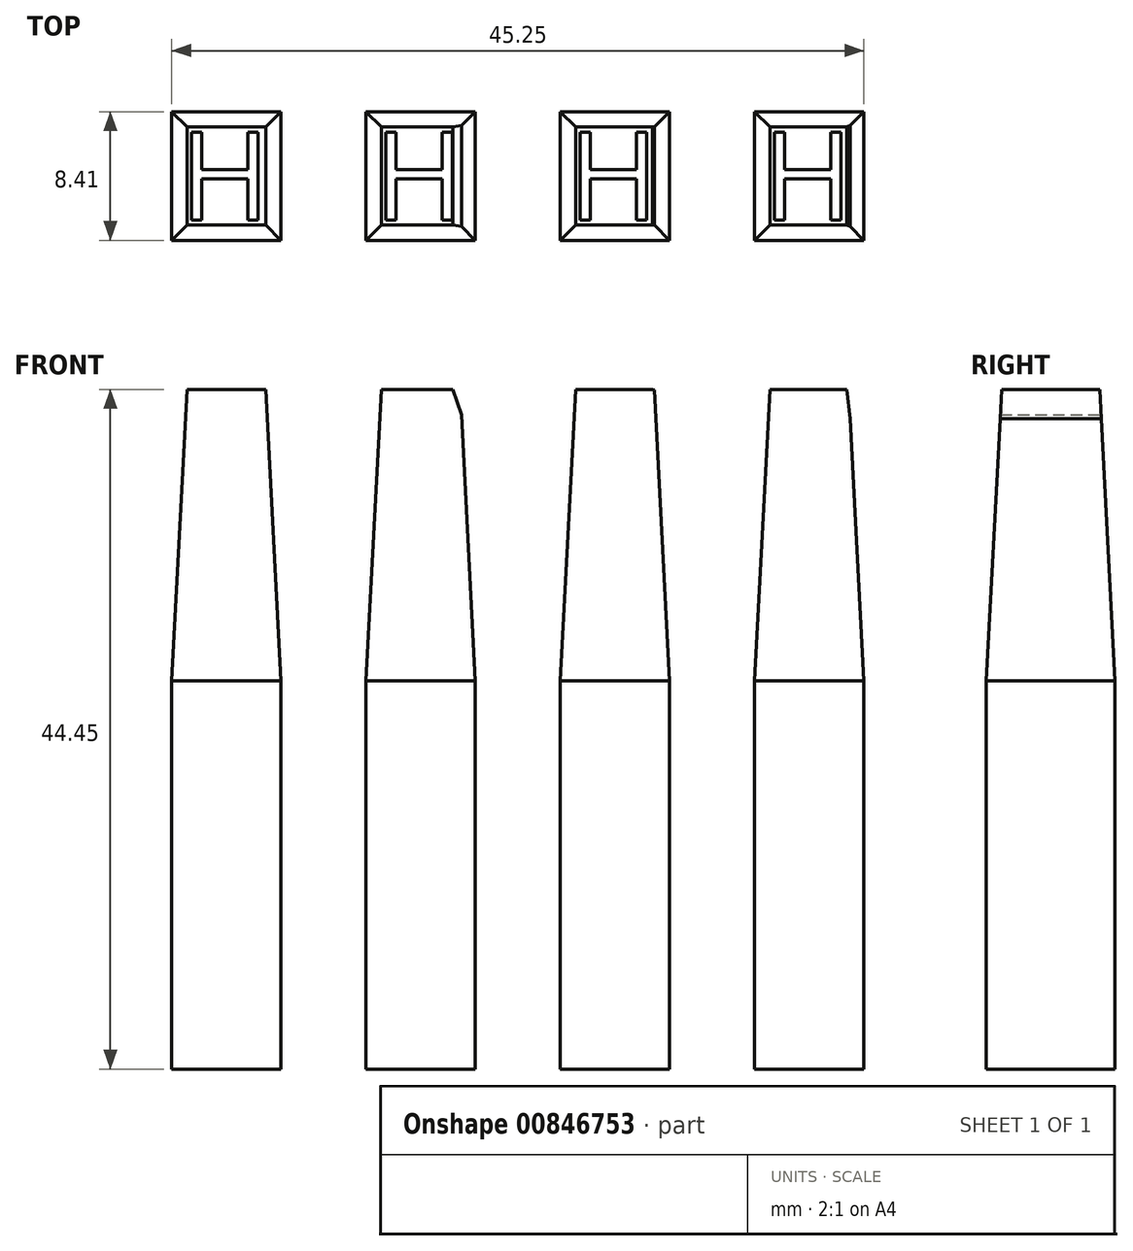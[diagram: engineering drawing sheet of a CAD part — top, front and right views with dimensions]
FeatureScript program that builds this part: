
annotation { "Feature Type Name" : "Feature", "Feature Type Description" : "" }
export const myFeature = defineFeature(function(context is Context, id is Id, definition is map)
    precondition{}
    {
        {
            var Q0;
            Q0=qCreatedBy(makeId("Top.planeOp"),FACE);
            var sketch = newSketch(context, id + "F0", { "sketchPlane" : qUnion([Q0])});
            skLineSegment(sketch, "E0.bottom", {"start": v(0, 0) * mm, "end": v(7.15, 0) * mm});
            skLineSegment(sketch, "E0.top", {"start": v(0, 8.41) * mm, "end": v(7.15, 8.41) * mm});
            skLineSegment(sketch, "E0.left", {"start": v(0, 0) * mm, "end": v(0, 8.41) * mm});
            skLineSegment(sketch, "E0.right", {"start": v(7.15, 0) * mm, "end": v(7.15, 8.41) * mm});
            skSolve(sketch);
        }
        {
            var Q0;
            Q0=makeQuery(id+"F0.imprint","IMPRINT",FACE,{"disambiguationData":[TD([[makeQuery(id+"F0.imprint","IMPRINT",EDGE,{"derivedFrom":sQuery(id+"F0.wireOp",EDGE,"E0.bottom")}),1.0]])]});
            extrude(context, id + "F1", {"entities" : qUnion([Q0]), "oppositeDirection" : true, "depth" : 25.4 * mm, "offsetDistance" : 25.4 * mm});
        }
        {
            var Q0;
            Q0=makeQuery(id+"F1.opExtrude","CAP_FACE",FACE,{"disambiguationData":[OSD([sQuery(id+"F0.wireOp",EDGE,"E0.bottom"),sQuery(id+"F0.wireOp",EDGE,"E0.top"),sQuery(id+"F0.wireOp",EDGE,"E0.left"),sQuery(id+"F0.wireOp",EDGE,"E0.right")])],"isStart":true});
            extrude(context, id + "F2", {"entities" : qUnion([Q0]), "operationType" : NewBodyOperationType.ADD, "depth" : 19.05 * mm, "offsetDistance" : 25.4 * mm, "hasDraft" : true, "draftAngle" : 3 * degree, "draftPullDirection" : true});
        }
        {
            var Q0;
            Q0=makeQuery(id+"F2.opExtrude","CAP_FACE",FACE,{"disambiguationData":[OSD([sQuery(id+"F0.wireOp",EDGE,"E0.bottom"),sQuery(id+"F0.wireOp",EDGE,"E0.top"),sQuery(id+"F0.wireOp",EDGE,"E0.left"),sQuery(id+"F0.wireOp",EDGE,"E0.right")])],"isStart":false});
            var sketch = newSketch(context, id + "F3", { "sketchPlane" : qUnion([Q0])});
            skText(sketch, "E1", { "text": "H", "fontName": "OpenSans-Regular.ttf"});
            const initialGuessF3  = {"E1": [0.00052, 0.00133, 1, 0, 0.00578]};
            skSetInitialGuess(sketch, initialGuessF3);
            skSolve(sketch);
        }
        {
            var Q0;
            Q0 = qSketchRegion(id + "F3", true);
            extrude(context, id + "F4", {"entities" : qUnion([Q0]), "operationType" : NewBodyOperationType.REMOVE, "oppositeDirection" : true, "depth" : 0 * mm, "offsetDistance" : 25.4 * mm});
        }
        {
            var Q0;
            Q0=makeQuery(id+"F2.opExtrude","CAP_FACE",FACE,{"disambiguationData":[OSD([sQuery(id+"F0.wireOp",EDGE,"E0.bottom"),sQuery(id+"F0.wireOp",EDGE,"E0.top"),sQuery(id+"F0.wireOp",EDGE,"E0.left"),sQuery(id+"F0.wireOp",EDGE,"E0.right")])],"isStart":false});
            cPlane(context, id + "F5", {"entities" : qUnion([Q0]), "cplaneType" : CPlaneType.OFFSET, "offset" : 1.9 * mm, "oppositeDirection" : true, "width" : 152.4 * mm, "height" : 152.4 * mm});
        }
        {
            var Q0;
            Q0=makeQuery(id+"F1.opExtrude","SWEPT_BODY",BODY,{"disambiguationData":[OSD([sQuery(id+"F0.wireOp",EDGE,"E0.bottom"),sQuery(id+"F0.wireOp",EDGE,"E0.top"),sQuery(id+"F0.wireOp",EDGE,"E0.left"),sQuery(id+"F0.wireOp",EDGE,"E0.right")])]});
            transform(context, id + "F6", {"entities" : qUnion([Q0]), "transformType" : TransformType.TRANSLATION_3D, "dx" : 12.7 * mm, "dy" : 0 * mm, "dz" : 0 * mm, "makeCopy" : true});
        }
        {
            var Q0;
            Q0=makeQuery(id+"F6.opPattern","COPY",BODY,{"derivedFrom":makeQuery(id+"F1.opExtrude","SWEPT_BODY",BODY,{"disambiguationData":[OSD([sQuery(id+"F0.wireOp",EDGE,"E0.bottom"),sQuery(id+"F0.wireOp",EDGE,"E0.top"),sQuery(id+"F0.wireOp",EDGE,"E0.left"),sQuery(id+"F0.wireOp",EDGE,"E0.right")])]}),"instanceName":"1"});
            deleteBodies(context, id + "F7", {"entities" : qUnion([Q0])});
        }
        {
            var Q0;
            Q0=makeQuery(id+"F1.opExtrude","SWEPT_BODY",BODY,{"disambiguationData":[OSD([sQuery(id+"F0.wireOp",EDGE,"E0.bottom"),sQuery(id+"F0.wireOp",EDGE,"E0.top"),sQuery(id+"F0.wireOp",EDGE,"E0.left"),sQuery(id+"F0.wireOp",EDGE,"E0.right")])]});
            transform(context, id + "F8", {"entities" : qUnion([Q0]), "transformType" : TransformType.TRANSLATION_3D, "dx" : 12.7 * mm, "dy" : 0 * mm, "dz" : 0 * mm, "makeCopy" : true});
        }
        {
            var Q0;
            Q0=qCreatedBy(makeId("Front.planeOp"),FACE);
            var sketch = newSketch(context, id + "F9", { "sketchPlane" : qUnion([Q0])});
            skLineSegment(sketch, "E2", {"start": v(18.36, 19.05) * mm, "end": v(19.03, 17.14) * mm});
            skLineSegment(sketch, "E3", {"start": v(19.03, 17.14) * mm, "end": v(19.03, 19.05) * mm});
            skLineSegment(sketch, "E4", {"start": v(19.03, 19.05) * mm, "end": v(18.36, 19.05) * mm});
            skPoint(sketch, "E5.0", {"position": v(18.36, 19.05) * mm});
            skSolve(sketch);
        }
        {
            var Q0;
            Q0 = qSketchRegion(id + "F9", true);
            extrude(context, id + "F10", {"entities" : qUnion([Q0]), "operationType" : NewBodyOperationType.REMOVE, "endBound" : BoundingType.THROUGH_ALL, "oppositeDirection" : true, "depth" : 25.4 * mm, "offsetDistance" : 25.4 * mm});
        }
        {
            var Q0;
            Q0=makeQuery(id+"F1.opExtrude","SWEPT_BODY",BODY,{"disambiguationData":[OSD([sQuery(id+"F0.wireOp",EDGE,"E0.bottom"),sQuery(id+"F0.wireOp",EDGE,"E0.top"),sQuery(id+"F0.wireOp",EDGE,"E0.left"),sQuery(id+"F0.wireOp",EDGE,"E0.right")])]});
            transform(context, id + "F11", {"entities" : qUnion([Q0]), "transformType" : TransformType.TRANSLATION_3D, "dx" : 25.4 * mm, "dy" : 0 * mm, "dz" : 0 * mm, "makeCopy" : true});
        }
        {
            var Q0;
            Q0=qCreatedBy(makeId("Front.planeOp"),FACE);
            var sketch = newSketch(context, id + "F12", { "sketchPlane" : qUnion([Q0])});
            skLineSegment(sketch, "E6", {"start": v(30.85, 19.19) * mm, "end": v(32.4, 18.82) * mm});
            skLineSegment(sketch, "E7", {"start": v(32.4, 18.82) * mm, "end": v(32.4, 19.27) * mm});
            skLineSegment(sketch, "E8", {"start": v(32.4, 19.27) * mm, "end": v(30.85, 19.19) * mm});
            skSolve(sketch);
        }
        {
            var Q0;
            Q0=makeQuery(id+"F12.imprint","IMPRINT",FACE,{"disambiguationData":[TD([[makeQuery(id+"F12.imprint","IMPRINT",EDGE,{"derivedFrom":sQuery(id+"F12.wireOp",EDGE,"E6")}),1.0]])]});
            extrude(context, id + "F13", {"entities" : qUnion([Q0]), "operationType" : NewBodyOperationType.REMOVE, "endBound" : BoundingType.THROUGH_ALL, "oppositeDirection" : true, "depth" : 25.4 * mm, "offsetDistance" : 25.4 * mm});
        }
        {
            var Q0;
            Q0=makeQuery(id+"F11.opPattern","COPY",BODY,{"derivedFrom":makeQuery(id+"F1.opExtrude","SWEPT_BODY",BODY,{"disambiguationData":[OSD([sQuery(id+"F0.wireOp",EDGE,"E0.bottom"),sQuery(id+"F0.wireOp",EDGE,"E0.top"),sQuery(id+"F0.wireOp",EDGE,"E0.left"),sQuery(id+"F0.wireOp",EDGE,"E0.right")])]}),"instanceName":"1"});
            transform(context, id + "F14", {"entities" : qUnion([Q0]), "transformType" : TransformType.TRANSLATION_3D, "dx" : 12.7 * mm, "dy" : 0 * mm, "dz" : 0 * mm, "makeCopy" : true});
        }
        {
            var Q0;
            Q0=qCreatedBy(makeId("Front.planeOp"),FACE);
            var sketch = newSketch(context, id + "F15", { "sketchPlane" : qUnion([Q0])});
            skLineSegment(sketch, "E9", {"start": v(44.12, 19.05) * mm, "end": v(44.35, 17.14) * mm});
            skLineSegment(sketch, "E10", {"start": v(44.35, 17.14) * mm, "end": v(44.35, 19.08) * mm});
            skLineSegment(sketch, "E11", {"start": v(44.35, 19.08) * mm, "end": v(44.12, 19.05) * mm});
            skPoint(sketch, "E12.0", {"position": v(44.12, 19.05) * mm});
            skLineSegment(sketch, "E13.0", {"start": v(44.25, 19.02) * mm, "end": v(45.25, 0) * mm});
            skSolve(sketch);
        }
        {
            var Q0;
            Q0=makeQuery(id+"F15.imprint","IMPRINT",FACE,{"disambiguationData":[TD([[makeQuery(id+"F15.imprint","IMPRINT",EDGE,{"derivedFrom":sQuery(id+"F15.wireOp",EDGE,"E9")}),1.0]])]});
            extrude(context, id + "F16", {"entities" : qUnion([Q0]), "operationType" : NewBodyOperationType.REMOVE, "endBound" : BoundingType.THROUGH_ALL, "oppositeDirection" : true, "depth" : 25.4 * mm, "offsetDistance" : 25.4 * mm});
        }
    });
